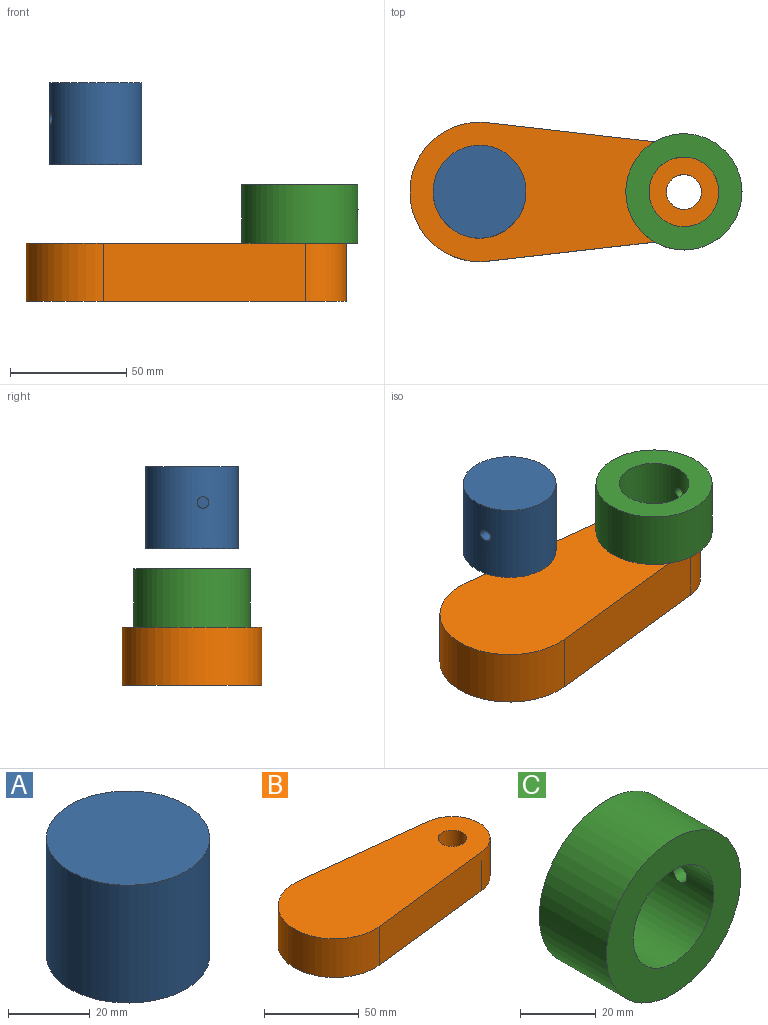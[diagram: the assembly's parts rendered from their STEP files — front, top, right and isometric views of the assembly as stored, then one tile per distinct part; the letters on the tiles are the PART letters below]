
ASSEMBLY  parts=3 mates=2
PART A: 5 faces, bbox 40x40x35.3 mm
  f0: cylinder r=20mm len=40mm, axis (0,0,1), area 4417.5mm2, adj f1,f2,f4
  f1: plane 40x40mm, normal (0,0,1), area 1256.6mm2, adj f0
  f2: plane 40x40mm, normal (0,0,-1), area 1256.6mm2, adj f0
  f3: plane 5x5mm, normal (1,0,0), area 19.6mm2, adj f4
  f4: cylinder r=2.5mm len=22.87mm, axis (-1,0,0), area 351mm2, adj f0,f3
PART B: 7 faces, bbox 137.9x60x25 mm
  f0: plane 86.77x25mm, normal (0.11,0.99,0), area 2183.4mm2, adj f1,f3,f4,f5
  f1: cylinder r=30mm len=60mm, axis (0,0,-1), area 2527.2mm2, adj f0,f2,f4,f5
  f2: plane 86.77x25mm, normal (0.11,-0.99,0), area 2183.4mm2, adj f1,f3,f4,f5
  f3: cylinder r=20mm len=39.74mm, axis (0,0,-1), area 1456.8mm2, adj f0,f2,f4,f5
  f4: plane 137.91x60mm, normal (0,0,1), area 6289mm2, adj f0,f1,f2,f3,f6
  f5: plane 137.91x60mm, normal (0,0,-1), area 6289mm2, adj f0,f1,f2,f3,f6
  f6: cylinder r=7.5mm len=25mm, axis (0,0,-1), area 1178.1mm2, adj f4,f5
PART C: 5 faces, bbox 50x25x50 mm
  f0: cylinder r=15mm len=30mm, axis (0,1,0), area 2336.4mm2, adj f2,f3,f4
  f1: cylinder r=25mm len=50mm, axis (0,1,0), area 3907.4mm2, adj f2,f3,f4
  f2: plane 50x50mm, normal (0,-1,0), area 1256.6mm2, adj f0,f1
  f3: plane 50x50mm, normal (0,1,0), area 1256.6mm2, adj f0,f1
  f4: cylinder r=2.5mm len=10.21mm, axis (-1,0,0), area 157.7mm2, adj f0,f1
PLACE A rot(axis=(0,0,-1),180deg) t=(-40.34,0,-41.39)mm
PLACE B at identity fixed
PLACE C rot(axis=(1,-0.03,-0.03),90deg) t=(44.57,0,50)mm
MATE revolute B.f3 <-> C.f1  axis (0,0,1) through (44.57,0,25)mm
MATE slider A.f0 <-> B.f1  axis (0,0,-1) through (-43.34,0,58.61)mm
